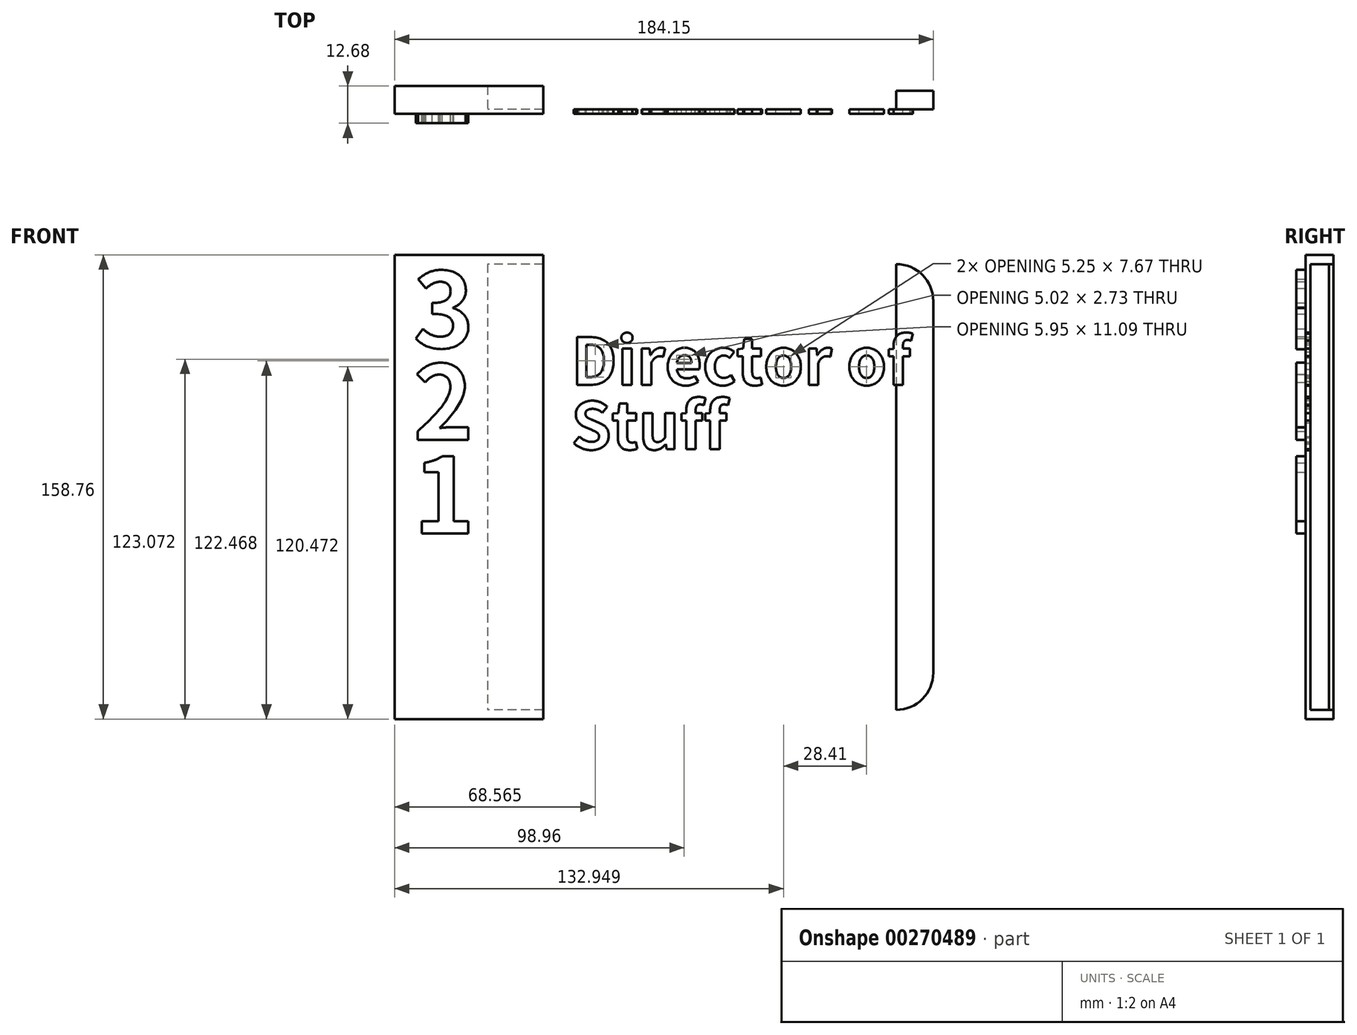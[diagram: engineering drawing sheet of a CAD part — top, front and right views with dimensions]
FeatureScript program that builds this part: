
annotation { "Feature Type Name" : "Feature", "Feature Type Description" : "" }
export const myFeature = defineFeature(function(context is Context, id is Id, definition is map)
    precondition{}
    {
        {
            var Q0;
            Q0=qCreatedBy(makeId("Front.planeOp"),FACE);
            var sketch = newSketch(context, id + "F0", { "sketchPlane" : qUnion([Q0])});
            skLineSegment(sketch, "E0.bottom", {"start": v(63.5, 76.2) * mm, "end": v(-76.2, 76.2) * mm});
            skLineSegment(sketch, "E0.top", {"start": v(63.5, -76.2) * mm, "end": v(-76.2, -76.2) * mm});
            skLineSegment(sketch, "E0.left", {"start": v(76.2, 63.5) * mm, "end": v(76.2, -63.5) * mm});
            skLineSegment(sketch, "E0.right", {"start": v(-76.2, 76.2) * mm, "end": v(-76.2, -76.2) * mm});
            skPoint(sketch, "E0.middle", {"position": v(0, 0) * mm});
            skPoint(sketch, "E1.visualSharp", {"position": v(76.2, 76.2) * mm});
            skArc(sketch, "E1.filletArc", {"start": v(76.2, 63.5) * mm, "mid": v(72.48, 72.48) * mm, "end": v(63.5, 76.2) * mm});
            skPoint(sketch, "E2.visualSharp", {"position": v(76.2, -76.2) * mm});
            skArc(sketch, "E2.filletArc", {"start": v(63.5, -76.2) * mm, "mid": v(72.48, -72.48) * mm, "end": v(76.2, -63.5) * mm});
            skSolve(sketch);
        }
        {
            var Q0;
            Q0 = qSketchRegion(id + "F0", true);
            extrude(context, id + "F1", {"entities" : qUnion([Q0]), "depth" : 6.35 * mm});
        }
        {
            var Q0;
            Q0=makeQuery(id+"F1.opExtrude","CAP_FACE",FACE,{"disambiguationData":[OSD([sQuery(id+"F0.wireOp",EDGE,"E0.bottom"),sQuery(id+"F0.wireOp",EDGE,"E0.top"),sQuery(id+"F0.wireOp",EDGE,"E0.left"),sQuery(id+"F0.wireOp",EDGE,"E0.right"),sQuery(id+"F0.wireOp",EDGE,"E1.filletArc"),sQuery(id+"F0.wireOp",EDGE,"E2.filletArc")])],"isStart":false});
            var sketch = newSketch(context, id + "F2", { "sketchPlane" : qUnion([Q0])});
            skLineSegment(sketch, "E3.bottom", {"start": v(-107.95, 79.38) * mm, "end": v(-57.15, 79.38) * mm});
            skLineSegment(sketch, "E3.top", {"start": v(-107.95, -79.38) * mm, "end": v(-57.15, -79.38) * mm});
            skLineSegment(sketch, "E3.left", {"start": v(-107.95, 79.38) * mm, "end": v(-107.95, -79.38) * mm});
            skLineSegment(sketch, "E3.right", {"start": v(-57.15, 79.38) * mm, "end": v(-57.15, -79.38) * mm});
            skSolve(sketch);
        }
        {
            var Q0;
            Q0 = qSketchRegion(id + "F2", true);
            extrude(context, id + "F3", {"entities" : qUnion([Q0]), "depth" : 1.59 * mm, "hasSecondDirection" : true, "secondDirectionOppositeDirection" : true, "secondDirectionDepth" : 7.92 * mm});
        }
        {
            var Q0;
            Q0=makeQuery(id+"F1.opExtrude","CAP_FACE",FACE,{"disambiguationData":[OSD([sQuery(id+"F0.wireOp",EDGE,"E0.bottom"),sQuery(id+"F0.wireOp",EDGE,"E0.top"),sQuery(id+"F0.wireOp",EDGE,"E0.left"),sQuery(id+"F0.wireOp",EDGE,"E0.right"),sQuery(id+"F0.wireOp",EDGE,"E1.filletArc"),sQuery(id+"F0.wireOp",EDGE,"E2.filletArc")])],"isStart":false});
            var sketch = newSketch(context, id + "F4", { "sketchPlane" : qUnion([Q0])});
            skLineSegment(sketch, "E4.0", {"start": v(-76.2, 76.2) * mm, "end": v(-76.2, -76.2) * mm});
            skLineSegment(sketch, "E4.1", {"start": v(63.5, 76.2) * mm, "end": v(-76.2, 76.2) * mm});
            skLineSegment(sketch, "E4.2", {"start": v(63.5, -76.2) * mm, "end": v(-76.2, -76.2) * mm});
            skLineSegment(sketch, "E5", {"start": v(63.5, 76.2) * mm, "end": v(63.5, -76.2) * mm});
            skSolve(sketch);
        }
        {
            var Q0;
            Q0 = qSketchRegion(id + "F4", true);
            extrude(context, id + "F5", {"entities" : qUnion([Q0]), "operationType" : NewBodyOperationType.REMOVE, "oppositeDirection" : true, "depth" : 25.4 * mm});
        }
        {
            var Q0;
            Q0=makeQuery(id+"F3.opExtrude","CAP_FACE",FACE,{"disambiguationData":[OSD([sQuery(id+"F2.wireOp",EDGE,"E3.bottom"),sQuery(id+"F2.wireOp",EDGE,"E3.top"),sQuery(id+"F2.wireOp",EDGE,"E3.left"),sQuery(id+"F2.wireOp",EDGE,"E3.right")])],"isStart":false});
            var sketch = newSketch(context, id + "F6", { "sketchPlane" : qUnion([Q0])});
            skText(sketch, "E6", { "text": "3", "fontName": "NotoSansCJKsc-Bold.otf"});
            skText(sketch, "E7", { "text": "2", "fontName": "NotoSansCJKsc-Bold.otf"});
            skText(sketch, "E8", { "text": "1", "fontName": "NotoSansCJKsc-Bold.otf"});
            const initialGuessF6  = {"E6": [-0.1016, 0.04763, 1, 0, 0.0254], "E7": [-0.1016, 0.01609, 1, 0, 0.02519], "E8": [-0.1016, -0.01597, 1, 0, 0.0257]};
            skSetInitialGuess(sketch, initialGuessF6);
            skSolve(sketch);
        }
        {
            var Q0;
            Q0 = qSketchRegion(id + "F6", true);
            extrude(context, id + "F7", {"entities" : qUnion([Q0]), "depth" : 3.17 * mm});
        }
        {
            var Q0;
            Q0=makeQuery(id+"F1.opExtrude","CAP_FACE",FACE,{"disambiguationData":[OSD([sQuery(id+"F0.wireOp",EDGE,"E0.bottom"),sQuery(id+"F0.wireOp",EDGE,"E0.top"),sQuery(id+"F0.wireOp",EDGE,"E0.left"),sQuery(id+"F0.wireOp",EDGE,"E0.right"),sQuery(id+"F0.wireOp",EDGE,"E1.filletArc"),sQuery(id+"F0.wireOp",EDGE,"E2.filletArc")])],"isStart":false});
            var sketch = newSketch(context, id + "F8", { "sketchPlane" : qUnion([Q0])});
            skText(sketch, "E9", { "text": "Director of\nStuff", "fontName": "NotoSansCJKsc-Bold.otf"});
            const initialGuessF8  = {"E9": [-0.04763, 0.03492, 1, 0, 0.01587]};
            skSetInitialGuess(sketch, initialGuessF8);
            skSolve(sketch);
        }
        {
            var Q0;
            Q0 = qSketchRegion(id + "F8", true);
            extrude(context, id + "F9", {"entities" : qUnion([Q0]), "depth" : 1.6 * mm});
        }
    });
